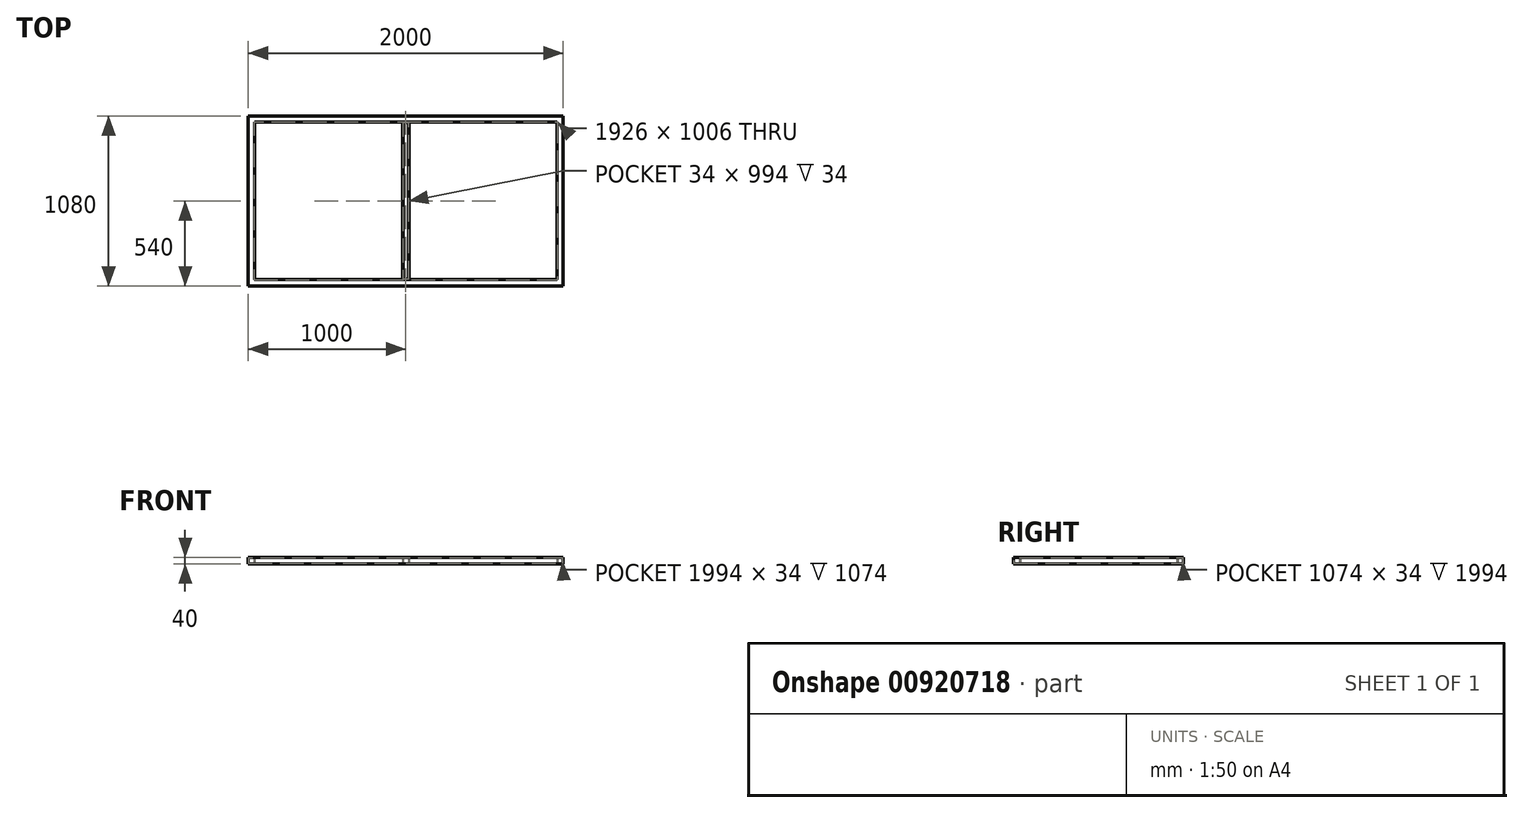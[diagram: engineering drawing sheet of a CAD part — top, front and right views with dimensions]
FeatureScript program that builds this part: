
annotation { "Feature Type Name" : "Feature", "Feature Type Description" : "" }
export const myFeature = defineFeature(function(context is Context, id is Id, definition is map)
    precondition{}
    {
        {
            var Q0;
            Q0=qCreatedBy(makeId("Top.planeOp"),FACE);
            var sketch = newSketch(context, id + "F0", { "sketchPlane" : qUnion([Q0])});
            skLineSegment(sketch, "E0.bottom", {"start": v(-20, 540) * mm, "end": v(20, 540) * mm});
            skLineSegment(sketch, "E0.top", {"start": v(-20, -540) * mm, "end": v(20, -540) * mm});
            skLineSegment(sketch, "E0.left", {"start": v(-20, 540) * mm, "end": v(-20, -540) * mm});
            skLineSegment(sketch, "E0.right", {"start": v(20, 540) * mm, "end": v(20, -540) * mm});
            skPoint(sketch, "E0.middle", {"position": v(0, 0) * mm});
            skLineSegment(sketch, "E1.bottom", {"start": v(-1000, 540) * mm, "end": v(1000, 540) * mm});
            skLineSegment(sketch, "E1.top", {"start": v(-1000, -540) * mm, "end": v(1000, -540) * mm});
            skLineSegment(sketch, "E1.left", {"start": v(-1000, 540) * mm, "end": v(-1000, -540) * mm});
            skLineSegment(sketch, "E1.right", {"start": v(1000, 540) * mm, "end": v(1000, -540) * mm});
            skLineSegment(sketch, "E2.bottom", {"start": v(-960, 500) * mm, "end": v(960, 500) * mm});
            skLineSegment(sketch, "E2.top", {"start": v(-960, -500) * mm, "end": v(960, -500) * mm});
            skLineSegment(sketch, "E2.left", {"start": v(-960, 500) * mm, "end": v(-960, -500) * mm});
            skLineSegment(sketch, "E2.right", {"start": v(960, 500) * mm, "end": v(960, -500) * mm});
            skSolve(sketch);
        }
        {
            var Q0;
            Q0 = qSketchRegion(id + "F0", true);
            var Q1;
            {var subQ0=sQuery(id+"F0.wireOp",EDGE,"E2.bottom");var subQ1=sQuery(id+"F0.wireOp",EDGE,"E0.left");var subQ2=makeQuery(id+"F0.imprint","INTERSECT",VERTEX,{"derivedFrom":[subQ1,subQ0]});Q1=makeQuery(id+"F0.imprint","IMPRINT",FACE,{"disambiguationData":[TD([[makeQuery(id+"F0.imprint","IMPRINT",EDGE,{"disambiguationData":[TD([[subQ2,-1.0]])],"derivedFrom":subQ1}),1.0]])]});}
            extrude(context, id + "F1", {"entities" : qUnion([Q0, Q1]), "depth" : 3 * mm, "offsetDistance" : 25 * mm});
        }
        {
            var Q0;
            Q0=makeQuery(id+"F1.opExtrude","CAP_FACE",FACE,{"disambiguationData":[OSD([sQuery(id+"F0.wireOp",EDGE,"E0.left"),sQuery(id+"F0.wireOp",EDGE,"E0.right"),sQuery(id+"F0.wireOp",EDGE,"E1.bottom"),sQuery(id+"F0.wireOp",EDGE,"E1.top"),sQuery(id+"F0.wireOp",EDGE,"E1.left"),sQuery(id+"F0.wireOp",EDGE,"E1.right"),sQuery(id+"F0.wireOp",EDGE,"E2.bottom"),sQuery(id+"F0.wireOp",EDGE,"E2.top"),sQuery(id+"F0.wireOp",EDGE,"E2.left"),sQuery(id+"F0.wireOp",EDGE,"E2.right")])],"isStart":false});
            var sketch = newSketch(context, id + "F2", { "sketchPlane" : qUnion([Q0])});
            skLineSegment(sketch, "E3.bottom", {"start": v(-997, 537) * mm, "end": v(997, 537) * mm});
            skLineSegment(sketch, "E3.top", {"start": v(-997, -537) * mm, "end": v(997, -537) * mm});
            skLineSegment(sketch, "E3.left", {"start": v(-997, 537) * mm, "end": v(-997, -537) * mm});
            skLineSegment(sketch, "E3.right", {"start": v(997, 537) * mm, "end": v(997, -537) * mm});
            skPoint(sketch, "E3.middle", {"position": v(0, 0) * mm});
            skLineSegment(sketch, "E4.bottom", {"start": v(-963, 503) * mm, "end": v(963, 503) * mm});
            skLineSegment(sketch, "E4.top", {"start": v(-963, -503) * mm, "end": v(963, -503) * mm});
            skLineSegment(sketch, "E4.left", {"start": v(-963, 503) * mm, "end": v(-963, -503) * mm});
            skLineSegment(sketch, "E4.right", {"start": v(963, 503) * mm, "end": v(963, -503) * mm});
            skLineSegment(sketch, "E5.bottom", {"start": v(-17, 497) * mm, "end": v(17, 497) * mm});
            skLineSegment(sketch, "E5.top", {"start": v(-17, -497) * mm, "end": v(17, -497) * mm});
            skLineSegment(sketch, "E5.left", {"start": v(-17, 497) * mm, "end": v(-17, -497) * mm});
            skLineSegment(sketch, "E5.right", {"start": v(17, 497) * mm, "end": v(17, -497) * mm});
            skLineSegment(sketch, "E6", {"start": v(20, 500) * mm, "end": v(-20, 500) * mm});
            skLineSegment(sketch, "E7", {"start": v(20, -500) * mm, "end": v(-20, -500) * mm});
            skSolve(sketch);
        }
        {
            var Q0;
            Q0=makeQuery(id+"F2.imprint","IMPRINT",FACE,{"disambiguationData":[TD([[makeQuery(id+"F2.imprint","IMPRINT",EDGE,{"derivedFrom":sQuery(id+"F2.wireOp",EDGE,"E4.bottom")}),-1.0]])]});
            var Q1;
            Q1=makeQuery(id+"F2.imprint","IMPRINT",FACE,{"disambiguationData":[TD([[makeQuery(id+"F2.imprint","IMPRINT",EDGE,{"derivedFrom":sQuery(id+"F2.wireOp",EDGE,"E5.bottom")}),1.0]])]});
            var Q2;
            Q2=makeQuery(id+"F2.imprint","IMPRINT",FACE,{"disambiguationData":[TD([[makeQuery(id+"F2.imprint","IMPRINT",EDGE,{"derivedFrom":sQuery(id+"F2.wireOp",EDGE,"E3.bottom")}),1.0]])]});
            extrude(context, id + "F3", {"entities" : qUnion([Q0, Q1, Q2]), "operationType" : NewBodyOperationType.ADD, "depth" : 34 * mm, "offsetDistance" : 25 * mm});
        }
        {
            var Q0;
            Q0=makeQuery(id+"F3.opExtrude","CAP_FACE",FACE,{"disambiguationData":[OSD([sQuery(id+"F0.wireOp",EDGE,"E0.left"),sQuery(id+"F0.wireOp",EDGE,"E0.right"),sQuery(id+"F0.wireOp",EDGE,"E2.bottom"),sQuery(id+"F0.wireOp",EDGE,"E2.top"),sQuery(id+"F0.wireOp",EDGE,"E2.left"),sQuery(id+"F0.wireOp",EDGE,"E2.right"),sQuery(id+"F2.wireOp",EDGE,"E4.bottom"),sQuery(id+"F2.wireOp",EDGE,"E4.top"),sQuery(id+"F2.wireOp",EDGE,"E4.left"),sQuery(id+"F2.wireOp",EDGE,"E4.right"),sQuery(id+"F2.wireOp",EDGE,"E5.bottom"),sQuery(id+"F2.wireOp",EDGE,"E5.top"),sQuery(id+"F2.wireOp",EDGE,"E5.left"),sQuery(id+"F2.wireOp",EDGE,"E5.right")])],"isStart":false});
            var sketch = newSketch(context, id + "F4", { "sketchPlane" : qUnion([Q0])});
            skLineSegment(sketch, "E8.bottom", {"start": v(-1000, 540) * mm, "end": v(1000, 540) * mm});
            skLineSegment(sketch, "E8.top", {"start": v(-1000, -540) * mm, "end": v(1000, -540) * mm});
            skLineSegment(sketch, "E8.left", {"start": v(-1000, 540) * mm, "end": v(-1000, -540) * mm});
            skLineSegment(sketch, "E8.right", {"start": v(1000, 540) * mm, "end": v(1000, -540) * mm});
            skPoint(sketch, "E8.middle", {"position": v(0, 0) * mm});
            skLineSegment(sketch, "E9.bottom", {"start": v(960, 500) * mm, "end": v(-960, 500) * mm});
            skLineSegment(sketch, "E9.top", {"start": v(960, -500) * mm, "end": v(-960, -500) * mm});
            skLineSegment(sketch, "E9.left", {"start": v(960, 500) * mm, "end": v(960, -500) * mm});
            skLineSegment(sketch, "E9.right", {"start": v(-960, 500) * mm, "end": v(-960, -500) * mm});
            skLineSegment(sketch, "E10.bottom", {"start": v(20, 500) * mm, "end": v(-20, 500) * mm});
            skLineSegment(sketch, "E10.top", {"start": v(20, -500) * mm, "end": v(-20, -500) * mm});
            skLineSegment(sketch, "E10.left", {"start": v(20, 500) * mm, "end": v(20, -500) * mm});
            skLineSegment(sketch, "E10.right", {"start": v(-20, 500) * mm, "end": v(-20, -500) * mm});
            skSolve(sketch);
        }
        {
            var Q0;
            Q0 = qSketchRegion(id + "F4", true);
            var Q1;
            Q1=makeQuery(id+"F4.imprint","IMPRINT",FACE,{"disambiguationData":[TD([[makeQuery(id+"F4.imprint","IMPRINT",EDGE,{"derivedFrom":makeQuery(id+"F3.opExtrude","CAP_EDGE",EDGE,{"disambiguationData":[OSD([sQuery(id+"F2.wireOp",EDGE,"E5.bottom")])],"isStart":false})}),-1.0]])]});
            var Q2;
            Q2=makeQuery(id+"F4.imprint","IMPRINT",FACE,{"disambiguationData":[TD([[makeQuery(id+"F4.imprint","IMPRINT",EDGE,{"derivedFrom":sQuery(id+"F4.wireOp",EDGE,"E10.bottom")}),1.0]])]});
            extrude(context, id + "F5", {"entities" : qUnion([Q0, Q1, Q2]), "operationType" : NewBodyOperationType.ADD, "depth" : 3 * mm, "offsetDistance" : 25 * mm});
        }
    });
